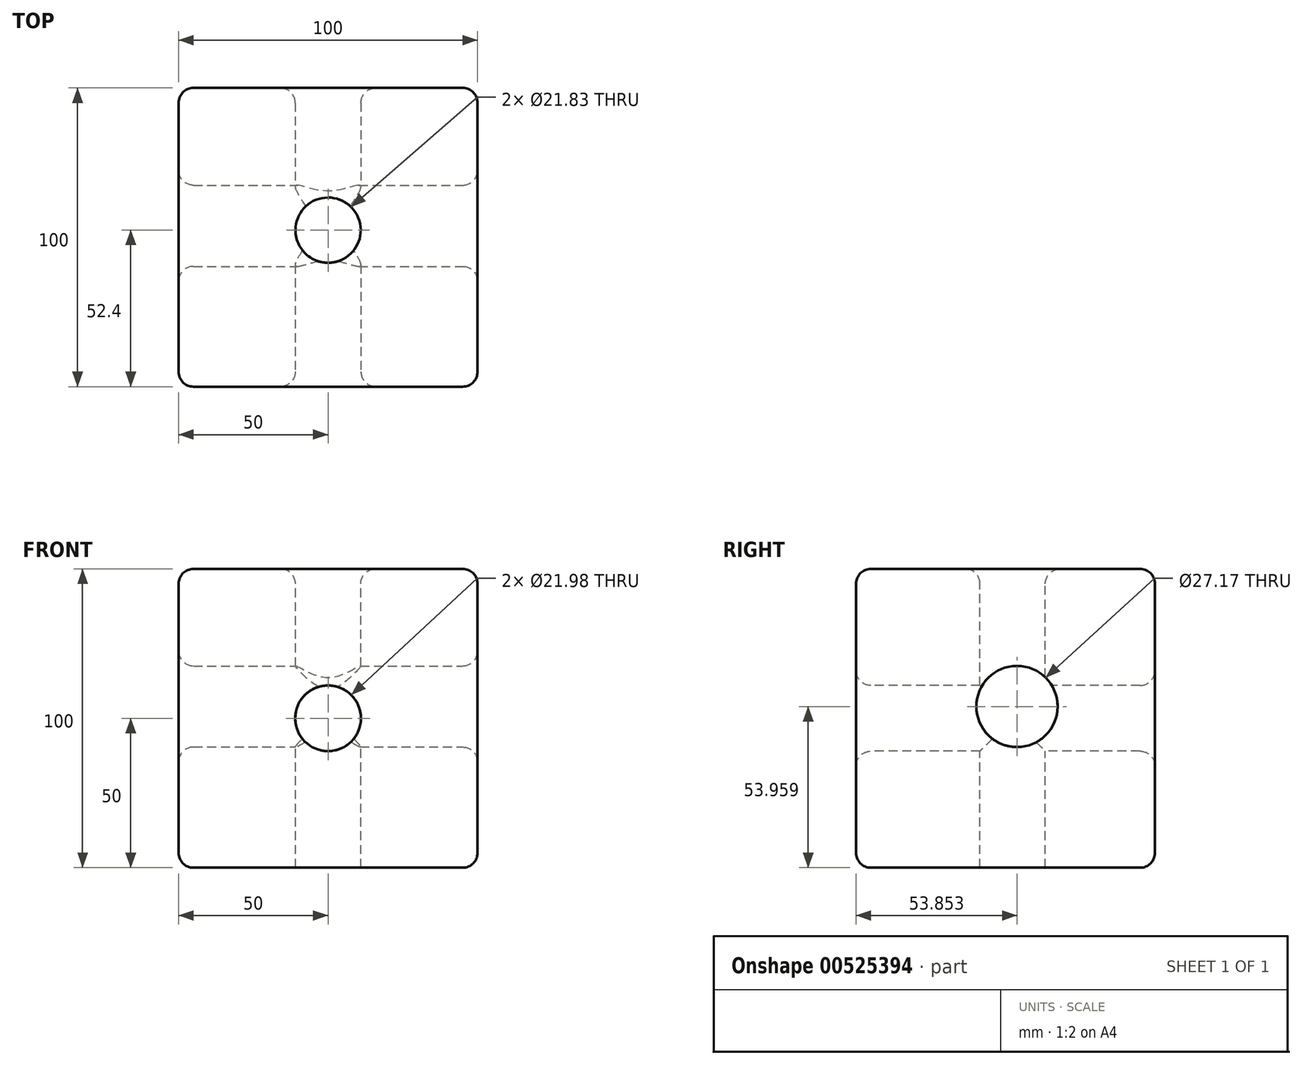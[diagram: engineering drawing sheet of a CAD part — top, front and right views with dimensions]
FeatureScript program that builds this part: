
annotation { "Feature Type Name" : "Feature", "Feature Type Description" : "" }
export const myFeature = defineFeature(function(context is Context, id is Id, definition is map)
    precondition{}
    {
        {
            var Q0;
            Q0=qCreatedBy(makeId("Front.planeOp"),FACE);
            var sketch = newSketch(context, id + "F0", { "sketchPlane" : qUnion([Q0])});
            skLineSegment(sketch, "E0.bottom", {"start": v(50, -50) * mm, "end": v(-50, -50) * mm});
            skLineSegment(sketch, "E0.top", {"start": v(50, 50) * mm, "end": v(-50, 50) * mm});
            skLineSegment(sketch, "E0.left", {"start": v(50, -50) * mm, "end": v(50, 50) * mm});
            skLineSegment(sketch, "E0.right", {"start": v(-50, -50) * mm, "end": v(-50, 50) * mm});
            skPoint(sketch, "E0.middle", {"position": v(0, 0) * mm});
            skSolve(sketch);
        }
        {
            var Q0;
            Q0=makeQuery(id+"F0.imprint","IMPRINT",FACE,{"disambiguationData":[TD([[makeQuery(id+"F0.imprint","IMPRINT",EDGE,{"derivedFrom":sQuery(id+"F0.wireOp",EDGE,"E0.bottom")}),-1.0]])]});
            extrude(context, id + "F1", {"entities" : qUnion([Q0]), "depth" : 100 * mm, "offsetDistance" : 25 * mm});
        }
        {
            var Q0;
            Q0=makeQuery(id+"F1.opExtrude","CAP_FACE",FACE,{"disambiguationData":[OSD([sQuery(id+"F0.wireOp",EDGE,"E0.bottom"),sQuery(id+"F0.wireOp",EDGE,"E0.top"),sQuery(id+"F0.wireOp",EDGE,"E0.left"),sQuery(id+"F0.wireOp",EDGE,"E0.right")])],"isStart":false});
            var sketch = newSketch(context, id + "F2", { "sketchPlane" : qUnion([Q0])});
            skCircle(sketch, "E1", {"center": v(0, 0) * mm, "radius": 11 * mm});
            skSolve(sketch);
        }
        {
            var Q0;
            Q0=makeQuery(id+"F2.imprint","IMPRINT",FACE,{"disambiguationData":[TD([[makeQuery(id+"F2.imprint","IMPRINT",EDGE,{"derivedFrom":sQuery(id+"F2.wireOp",EDGE,"E1")}),1.0]])]});
            var Q1;
            Q1=makeQuery(id+"F1.opExtrude","CAP_FACE",FACE,{"disambiguationData":[OSD([sQuery(id+"F0.wireOp",EDGE,"E0.bottom"),sQuery(id+"F0.wireOp",EDGE,"E0.top"),sQuery(id+"F0.wireOp",EDGE,"E0.left"),sQuery(id+"F0.wireOp",EDGE,"E0.right")])],"isStart":true});
            extrude(context, id + "F3", {"entities" : qUnion([Q0]), "operationType" : NewBodyOperationType.REMOVE, "endBound" : BoundingType.UP_TO_SURFACE, "oppositeDirection" : true, "depth" : 14 * mm, "endBoundEntityFace" : qUnion([Q1]), "offsetDistance" : 25 * mm});
        }
        {
            var Q0;
            Q0=makeQuery(id+"F1.opExtrude","SWEPT_FACE",FACE,{"disambiguationData":[OSD([sQuery(id+"F0.wireOp",EDGE,"E0.top")])]});
            var sketch = newSketch(context, id + "F4", { "sketchPlane" : qUnion([Q0])});
            skCircle(sketch, "E2", {"center": v(0, -47.6) * mm, "radius": 10.92 * mm});
            skSolve(sketch);
        }
        {
            var Q0;
            Q0 = qSketchRegion(id + "F4", true);
            var Q1;
            Q1=makeQuery(id+"F1.opExtrude","SWEPT_FACE",FACE,{"disambiguationData":[OSD([sQuery(id+"F0.wireOp",EDGE,"E0.bottom")])]});
            extrude(context, id + "F5", {"entities" : qUnion([Q0]), "operationType" : NewBodyOperationType.REMOVE, "endBound" : BoundingType.UP_TO_SURFACE, "oppositeDirection" : true, "depth" : 21 * mm, "endBoundEntityFace" : qUnion([Q1]), "offsetDistance" : 25 * mm});
        }
        {
            var Q0;
            Q0=makeQuery(id+"F1.opExtrude","SWEPT_FACE",FACE,{"disambiguationData":[OSD([sQuery(id+"F0.wireOp",EDGE,"E0.left")])]});
            var sketch = newSketch(context, id + "F6", { "sketchPlane" : qUnion([Q0])});
            skCircle(sketch, "E3", {"center": v(-46.15, 3.96) * mm, "radius": 13.58 * mm});
            skSolve(sketch);
        }
        {
            var Q0;
            Q0 = qSketchRegion(id + "F6", true);
            var Q1;
            Q1=makeQuery(id+"F1.opExtrude","SWEPT_FACE",FACE,{"disambiguationData":[OSD([sQuery(id+"F0.wireOp",EDGE,"E0.right")])]});
            extrude(context, id + "F7", {"entities" : qUnion([Q0]), "operationType" : NewBodyOperationType.REMOVE, "endBound" : BoundingType.UP_TO_SURFACE, "oppositeDirection" : true, "depth" : 13 * mm, "endBoundEntityFace" : qUnion([Q1]), "offsetDistance" : 25 * mm});
        }
        {
            var Q0;
            Q0=makeQuery(id+"F1.opExtrude","CAP_FACE",FACE,{"disambiguationData":[OSD([sQuery(id+"F0.wireOp",EDGE,"E0.bottom"),sQuery(id+"F0.wireOp",EDGE,"E0.top"),sQuery(id+"F0.wireOp",EDGE,"E0.left"),sQuery(id+"F0.wireOp",EDGE,"E0.right")])],"isStart":false});
            fillet(context, id + "F8", {"entities" : qUnion([Q0]), "radius" : 5 * mm, "tangentPropagation" : true, "allowEdgeOverflow" : false});
        }
        {
            var Q0;
            Q0=makeQuery(id+"F1.opExtrude","SWEPT_FACE",FACE,{"disambiguationData":[OSD([sQuery(id+"F0.wireOp",EDGE,"E0.right")])]});
            fillet(context, id + "F9", {"entities" : qUnion([Q0]), "radius" : 5 * mm, "tangentPropagation" : true, "allowEdgeOverflow" : false});
        }
        {
            var Q0;
            Q0=makeQuery(id+"F1.opExtrude","SWEPT_FACE",FACE,{"disambiguationData":[OSD([sQuery(id+"F0.wireOp",EDGE,"E0.left")])]});
            fillet(context, id + "F10", {"entities" : qUnion([Q0]), "radius" : 5 * mm, "tangentPropagation" : true, "allowEdgeOverflow" : false});
        }
        {
            var Q0;
            Q0=makeQuery(id+"F1.opExtrude","CAP_FACE",FACE,{"disambiguationData":[OSD([sQuery(id+"F0.wireOp",EDGE,"E0.bottom"),sQuery(id+"F0.wireOp",EDGE,"E0.top"),sQuery(id+"F0.wireOp",EDGE,"E0.left"),sQuery(id+"F0.wireOp",EDGE,"E0.right")])],"isStart":true});
            var Q1;
            Q1=makeQuery(id+"F5.boolean.opBoolean","COPY",EDGE,{"derivedFrom":makeQuery(id+"F5.opExtrude","CAP_EDGE",EDGE,{"disambiguationData":[OSD([sQuery(id+"F4.wireOp",EDGE,"E2")])],"isStart":false})});
            var Q2;
            Q2=makeQuery(id+"F1.opExtrude","SWEPT_FACE",FACE,{"disambiguationData":[OSD([sQuery(id+"F0.wireOp",EDGE,"E0.top")])]});
            fillet(context, id + "F11", {"entities" : qUnion([Q0, Q1, Q2]), "radius" : 5 * mm, "tangentPropagation" : true, "allowEdgeOverflow" : false});
        }
    });
